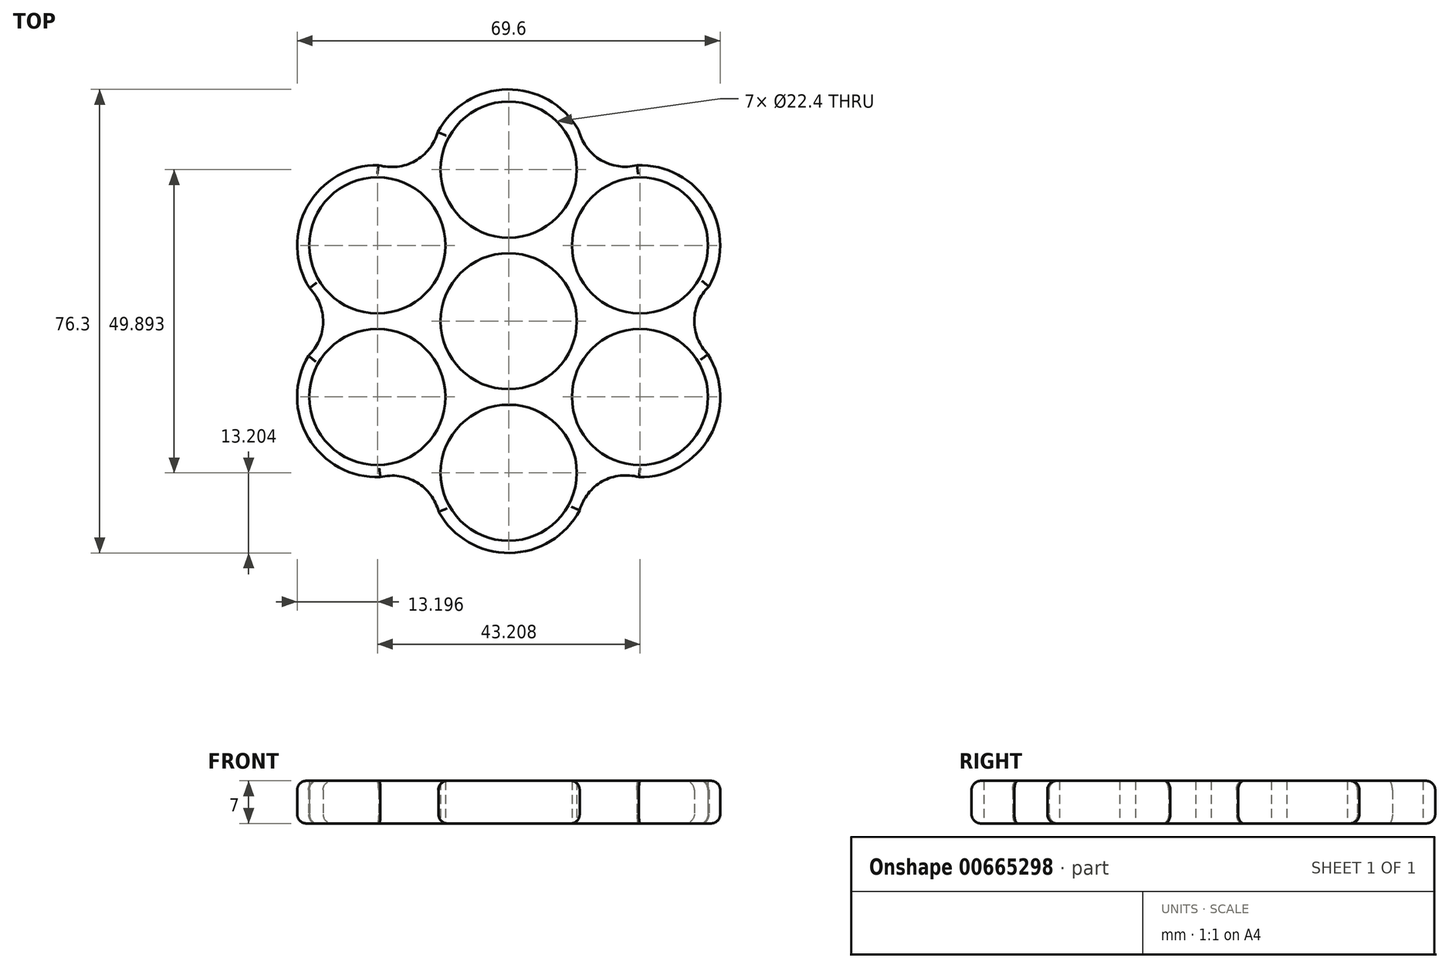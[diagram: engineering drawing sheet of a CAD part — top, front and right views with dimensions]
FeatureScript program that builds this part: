
annotation { "Feature Type Name" : "Feature", "Feature Type Description" : "" }
export const myFeature = defineFeature(function(context is Context, id is Id, definition is map)
    precondition{}
    {
        {
            var Q0;
            Q0=qCreatedBy(makeId("Top.planeOp"),FACE);
            var sketch = newSketch(context, id + "F0", { "sketchPlane" : qUnion([Q0])});
            skCircle(sketch, "E0", {"center": v(0, 0) * mm, "radius": 11.2 * mm});
            skCircle(sketch, "E1", {"center": v(0, 24.95) * mm, "radius": 11.2 * mm});
            skArc(sketch, "E2", {"start": v(12.56, 29) * mm, "mid": v(0.1, 38.15) * mm, "end": v(-12.5, 29.2) * mm});
            skCircle(sketch, "E3.1.0", {"center": v(-21.6, 12.47) * mm, "radius": 11.2 * mm});
            skArc(sketch, "E3.1.1", {"start": v(-18.84, 25.38) * mm, "mid": v(-32.98, 19.16) * mm, "end": v(-31.54, 3.78) * mm});
            skCircle(sketch, "E3.2.0", {"center": v(-21.6, -12.47) * mm, "radius": 11.2 * mm});
            skArc(sketch, "E3.2.1", {"start": v(-31.4, -3.62) * mm, "mid": v(-33.09, -18.98) * mm, "end": v(-19.04, -25.42) * mm});
            skCircle(sketch, "E3.3.0", {"center": v(0, -24.95) * mm, "radius": 11.2 * mm});
            skArc(sketch, "E3.3.1", {"start": v(-12.56, -29) * mm, "mid": v(-0.1, -38.15) * mm, "end": v(12.5, -29.2) * mm});
            skCircle(sketch, "E3.4.0", {"center": v(21.6, -12.47) * mm, "radius": 11.2 * mm});
            skCircle(sketch, "E3.5.0", {"center": v(21.6, 12.47) * mm, "radius": 11.2 * mm});
            skArc(sketch, "E3.5.1", {"start": v(31.4, 3.62) * mm, "mid": v(33.09, 18.98) * mm, "end": v(19.04, 25.42) * mm});
            skArc(sketch, "E4", {"start": v(-32.94, -5.7) * mm, "mid": v(-30.54, -0.17) * mm, "end": v(-32.78, 5.44) * mm});
            skArc(sketch, "E5.1.0", {"start": v(-11.53, -31.38) * mm, "mid": v(-15.13, -26.53) * mm, "end": v(-21.1, -25.66) * mm});
            skArc(sketch, "E5.2.0", {"start": v(21.41, -25.67) * mm, "mid": v(15.42, -26.37) * mm, "end": v(11.67, -31.1) * mm});
            skArc(sketch, "E5.3.0", {"start": v(32.94, 5.7) * mm, "mid": v(30.54, 0.17) * mm, "end": v(32.78, -5.44) * mm});
            skArc(sketch, "E5.4.0", {"start": v(11.53, 31.38) * mm, "mid": v(15.13, 26.53) * mm, "end": v(21.1, 25.66) * mm});
            skArc(sketch, "E5.5.0", {"start": v(-21.41, 25.67) * mm, "mid": v(-15.42, 26.37) * mm, "end": v(-11.67, 31.1) * mm});
            skArc(sketch, "E6.trimOffspring", {"start": v(18.84, -25.38) * mm, "mid": v(32.98, -19.16) * mm, "end": v(31.54, -3.78) * mm});
            skSolve(sketch);
        }
        {
            var Q0;
            Q0=makeQuery(id+"F0.imprint","IMPRINT",FACE,{"disambiguationData":[TD([[makeQuery(id+"F0.imprint","IMPRINT",EDGE,{"derivedFrom":sQuery(id+"F0.wireOp",EDGE,"E0")}),-1.0]])]});
            extrude(context, id + "F1", {"entities" : qUnion([Q0]), "depth" : 7 * mm, "offsetDistance" : 25 * mm});
        }
        {
            var Q0;
            Q0=makeQuery(id+"F1.opExtrude","CAP_EDGE",EDGE,{"disambiguationData":[OSD([sQuery(id+"F0.wireOp",EDGE,"E5.2.0")])],"isStart":false});
            var Q1;
            Q1=makeQuery(id+"F1.opExtrude","CAP_EDGE",EDGE,{"disambiguationData":[OSD([sQuery(id+"F0.wireOp",EDGE,"E6.trimOffspring")])],"isStart":false});
            var Q2;
            Q2=makeQuery(id+"F1.opExtrude","CAP_EDGE",EDGE,{"disambiguationData":[OSD([sQuery(id+"F0.wireOp",EDGE,"E5.3.0")])],"isStart":false});
            var Q3;
            Q3=makeQuery(id+"F1.opExtrude","CAP_EDGE",EDGE,{"disambiguationData":[OSD([sQuery(id+"F0.wireOp",EDGE,"E3.5.1")])],"isStart":false});
            var Q4;
            Q4=makeQuery(id+"F1.opExtrude","SWEPT_EDGE",EDGE,{"disambiguationData":[OSD([sQuery(id+"F0.wireOp",EDGE,"E2"),sQuery(id+"F0.wireOp",EDGE,"E5.4.0")])]});
            var Q5;
            Q5=makeQuery(id+"F1.opExtrude","CAP_EDGE",EDGE,{"disambiguationData":[OSD([sQuery(id+"F0.wireOp",EDGE,"E2")])],"isStart":false});
            var Q6;
            Q6=makeQuery(id+"F1.opExtrude","CAP_EDGE",EDGE,{"disambiguationData":[OSD([sQuery(id+"F0.wireOp",EDGE,"E5.5.0")])],"isStart":false});
            var Q7;
            Q7=makeQuery(id+"F1.opExtrude","CAP_EDGE",EDGE,{"disambiguationData":[OSD([sQuery(id+"F0.wireOp",EDGE,"E3.1.1")])],"isStart":false});
            var Q8;
            Q8=makeQuery(id+"F1.opExtrude","CAP_EDGE",EDGE,{"disambiguationData":[OSD([sQuery(id+"F0.wireOp",EDGE,"E4")])],"isStart":false});
            var Q9;
            Q9=makeQuery(id+"F1.opExtrude","CAP_EDGE",EDGE,{"disambiguationData":[OSD([sQuery(id+"F0.wireOp",EDGE,"E3.2.1")])],"isStart":false});
            var Q10;
            Q10=makeQuery(id+"F1.opExtrude","CAP_EDGE",EDGE,{"disambiguationData":[OSD([sQuery(id+"F0.wireOp",EDGE,"E3.3.1")])],"isStart":false});
            var Q11;
            Q11=makeQuery(id+"F1.opExtrude","CAP_EDGE",EDGE,{"disambiguationData":[OSD([sQuery(id+"F0.wireOp",EDGE,"E5.1.0")])],"isStart":false});
            var Q12;
            Q12=makeQuery(id+"F1.opExtrude","CAP_EDGE",EDGE,{"disambiguationData":[OSD([sQuery(id+"F0.wireOp",EDGE,"E5.4.0")])],"isStart":false});
            var Q13;
            Q13=makeQuery(id+"F1.opExtrude","CAP_EDGE",EDGE,{"disambiguationData":[OSD([sQuery(id+"F0.wireOp",EDGE,"E6.trimOffspring")])],"isStart":true});
            var Q14;
            Q14=makeQuery(id+"F1.opExtrude","CAP_EDGE",EDGE,{"disambiguationData":[OSD([sQuery(id+"F0.wireOp",EDGE,"E5.2.0")])],"isStart":true});
            var Q15;
            Q15=makeQuery(id+"F1.opExtrude","CAP_EDGE",EDGE,{"disambiguationData":[OSD([sQuery(id+"F0.wireOp",EDGE,"E3.3.1")])],"isStart":true});
            var Q16;
            Q16=makeQuery(id+"F1.opExtrude","CAP_EDGE",EDGE,{"disambiguationData":[OSD([sQuery(id+"F0.wireOp",EDGE,"E5.1.0")])],"isStart":true});
            var Q17;
            Q17=makeQuery(id+"F1.opExtrude","CAP_EDGE",EDGE,{"disambiguationData":[OSD([sQuery(id+"F0.wireOp",EDGE,"E3.2.1")])],"isStart":true});
            var Q18;
            Q18=makeQuery(id+"F1.opExtrude","CAP_EDGE",EDGE,{"disambiguationData":[OSD([sQuery(id+"F0.wireOp",EDGE,"E4")])],"isStart":true});
            var Q19;
            Q19=makeQuery(id+"F1.opExtrude","CAP_EDGE",EDGE,{"disambiguationData":[OSD([sQuery(id+"F0.wireOp",EDGE,"E3.1.1")])],"isStart":true});
            var Q20;
            Q20=makeQuery(id+"F1.opExtrude","CAP_EDGE",EDGE,{"disambiguationData":[OSD([sQuery(id+"F0.wireOp",EDGE,"E5.5.0")])],"isStart":true});
            var Q21;
            Q21=makeQuery(id+"F1.opExtrude","CAP_EDGE",EDGE,{"disambiguationData":[OSD([sQuery(id+"F0.wireOp",EDGE,"E2")])],"isStart":true});
            var Q22;
            Q22=makeQuery(id+"F1.opExtrude","CAP_EDGE",EDGE,{"disambiguationData":[OSD([sQuery(id+"F0.wireOp",EDGE,"E3.5.1")])],"isStart":true});
            var Q23;
            Q23=makeQuery(id+"F1.opExtrude","CAP_EDGE",EDGE,{"disambiguationData":[OSD([sQuery(id+"F0.wireOp",EDGE,"E5.4.0")])],"isStart":true});
            var Q24;
            Q24=makeQuery(id+"F1.opExtrude","CAP_EDGE",EDGE,{"disambiguationData":[OSD([sQuery(id+"F0.wireOp",EDGE,"E5.3.0")])],"isStart":true});
            fillet(context, id + "F2", {"entities" : qUnion([Q0, Q1, Q2, Q3, Q4, Q5, Q6, Q7, Q8, Q9, Q10, Q11, Q12, Q13, Q14, Q15, Q16, Q17, Q18, Q19, Q20, Q21, Q22, Q23, Q24]), "radius" : 1.5 * mm, "tangentPropagation" : true, "allowEdgeOverflow" : false});
        }
    });
